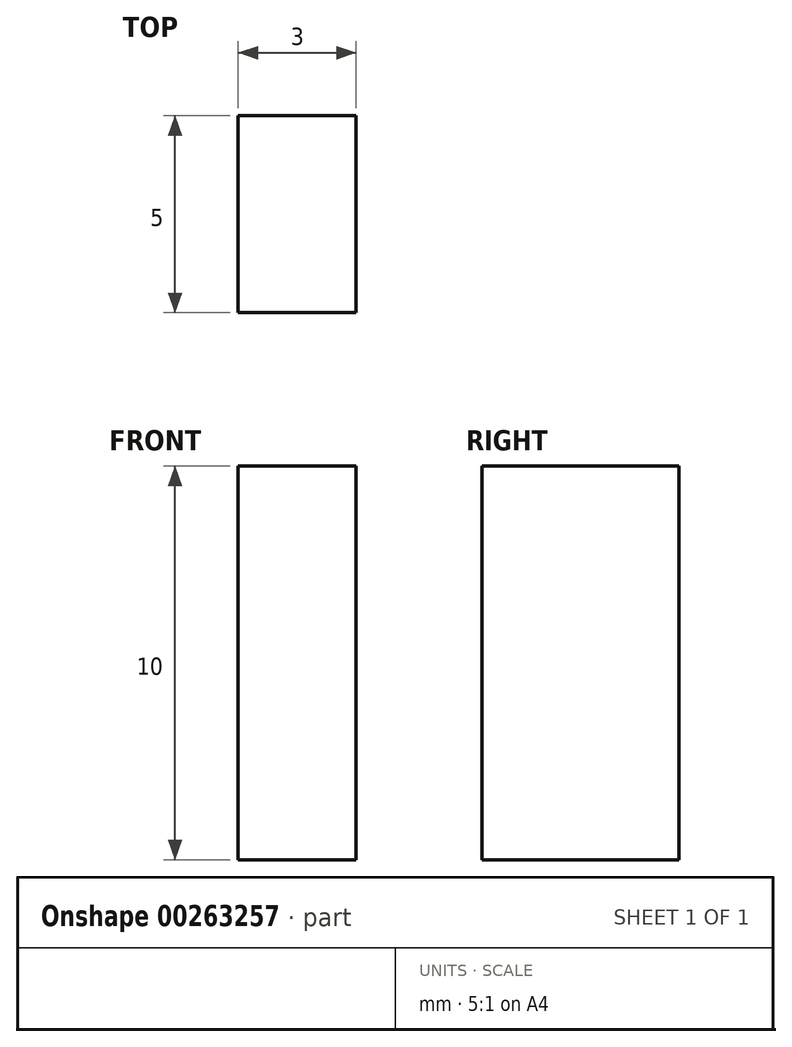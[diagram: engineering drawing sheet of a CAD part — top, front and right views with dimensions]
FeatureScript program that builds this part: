
annotation { "Feature Type Name" : "Feature", "Feature Type Description" : "" }
export const myFeature = defineFeature(function(context is Context, id is Id, definition is map)
    precondition{}
    {
        {
            var Q0;
            Q0=qCreatedBy(makeId("Front.planeOp"),FACE);
            var sketch = newSketch(context, id + "F0", { "sketchPlane" : qUnion([Q0])});
            skLineSegment(sketch, "E0.bottom", {"start": v(1.5, -5) * mm, "end": v(-1.5, -5) * mm});
            skLineSegment(sketch, "E0.top", {"start": v(1.5, 5) * mm, "end": v(-1.5, 5) * mm});
            skLineSegment(sketch, "E0.left", {"start": v(1.5, -5) * mm, "end": v(1.5, 5) * mm});
            skLineSegment(sketch, "E0.right", {"start": v(-1.5, -5) * mm, "end": v(-1.5, 5) * mm});
            skPoint(sketch, "E0.middle", {"position": v(0, 0) * mm});
            skSolve(sketch);
        }
        {
            var Q0;
            Q0 = qSketchRegion(id + "F0", true);
            extrude(context, id + "F1", {"entities" : qUnion([Q0]), "depth" : 5 * mm});
        }
    });
